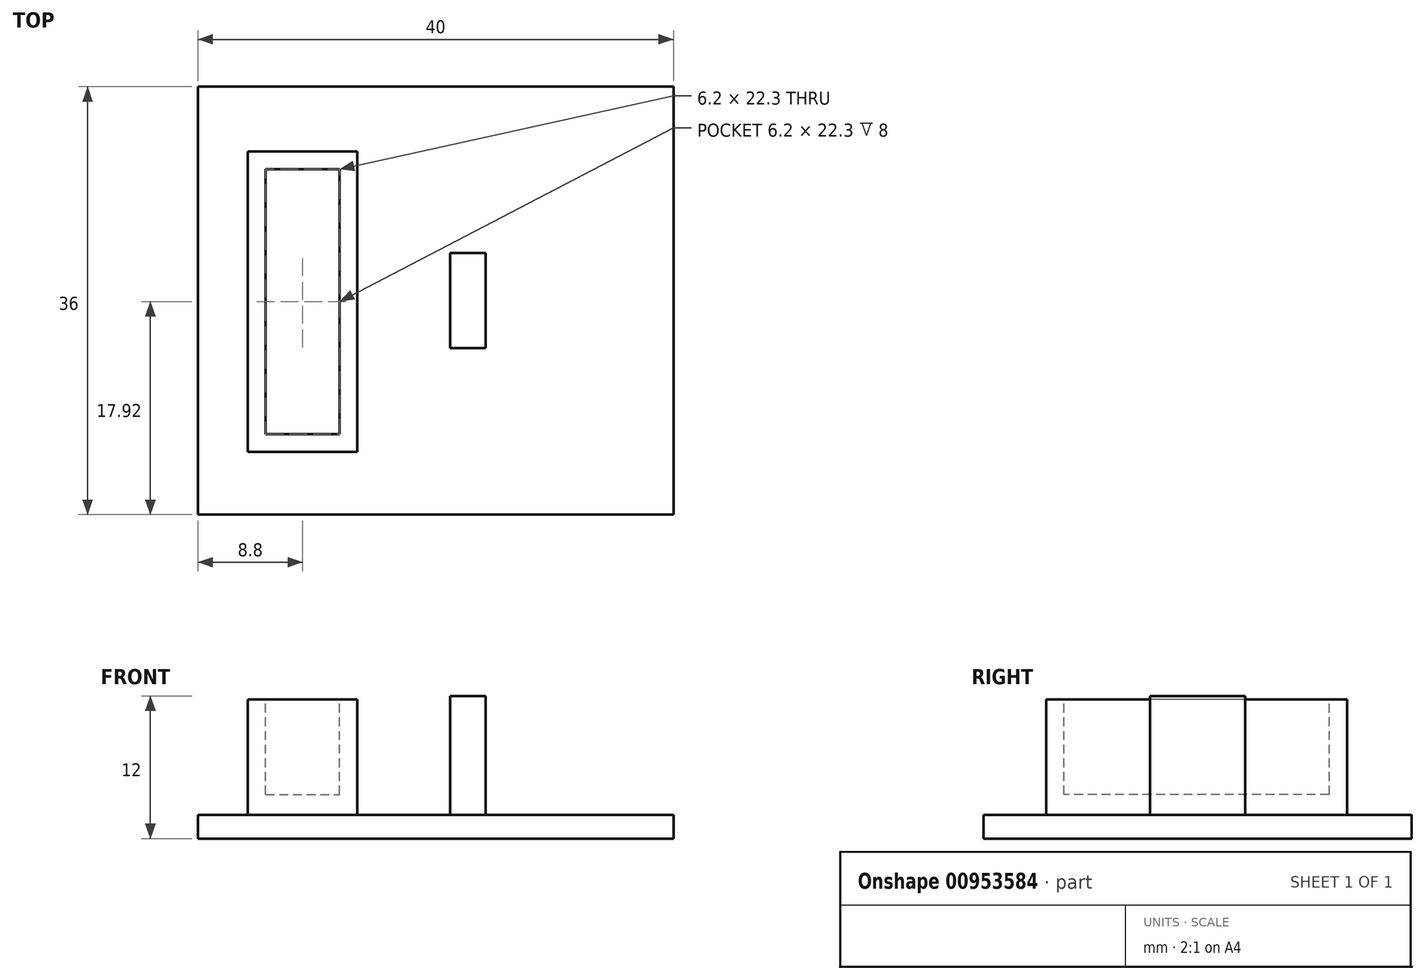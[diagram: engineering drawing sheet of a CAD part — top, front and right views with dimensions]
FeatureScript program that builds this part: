
annotation { "Feature Type Name" : "Feature", "Feature Type Description" : "" }
export const myFeature = defineFeature(function(context is Context, id is Id, definition is map)
    precondition{}
    {
        {
            var Q0;
            Q0=qCreatedBy(makeId("Top.planeOp"),FACE);
            var sketch = newSketch(context, id + "F0", { "sketchPlane" : qUnion([Q0])});
            skLineSegment(sketch, "E0.bottom", {"start": v(-20, 18) * mm, "end": v(20, 18) * mm});
            skLineSegment(sketch, "E0.top", {"start": v(-20, -18) * mm, "end": v(20, -18) * mm});
            skLineSegment(sketch, "E0.left", {"start": v(-20, 18) * mm, "end": v(-20, -18) * mm});
            skLineSegment(sketch, "E0.right", {"start": v(20, 18) * mm, "end": v(20, -18) * mm});
            skLineSegment(sketch, "E1", {"start": v(20, 18) * mm, "end": v(-20, -18) * mm, "construction": true});
            skLineSegment(sketch, "E2", {"start": v(-20, 18) * mm, "end": v(20, -18) * mm, "construction": true});
            skPoint(sketch, "E3", {"position": v(0, 0) * mm});
            skSolve(sketch);
        }
        {
            var Q0;
            Q0 = qSketchRegion(id + "F0", true);
            extrude(context, id + "F1", {"entities" : qUnion([Q0]), "depth" : 2 * mm, "offsetDistance" : 25 * mm});
        }
        {
            var Q0;
            Q0=makeQuery(id+"F1.opExtrude","CAP_FACE",FACE,{"disambiguationData":[OSD([sQuery(id+"F0.wireOp",EDGE,"E0.bottom"),sQuery(id+"F0.wireOp",EDGE,"E0.top"),sQuery(id+"F0.wireOp",EDGE,"E0.left"),sQuery(id+"F0.wireOp",EDGE,"E0.right")])],"isStart":false});
            var sketch = newSketch(context, id + "F2", { "sketchPlane" : qUnion([Q0])});
            skLineSegment(sketch, "E4.bottom", {"start": v(-15.8, 12.57) * mm, "end": v(-6.6, 12.57) * mm});
            skLineSegment(sketch, "E4.top", {"start": v(-15.8, -12.73) * mm, "end": v(-6.6, -12.73) * mm});
            skLineSegment(sketch, "E4.left", {"start": v(-15.8, 12.57) * mm, "end": v(-15.8, -12.73) * mm});
            skLineSegment(sketch, "E4.right", {"start": v(-6.6, 12.57) * mm, "end": v(-6.6, -12.73) * mm});
            skSolve(sketch);
        }
        {
            var Q0;
            Q0 = qSketchRegion(id + "F2", true);
            extrude(context, id + "F3", {"entities" : qUnion([Q0]), "depth" : 9.7 * mm, "offsetDistance" : 25 * mm});
        }
        {
            var Q0;
            Q0=makeQuery(id+"F3.opExtrude","CAP_FACE",FACE,{"disambiguationData":[OSD([sQuery(id+"F2.wireOp",EDGE,"E4.bottom"),sQuery(id+"F2.wireOp",EDGE,"E4.top"),sQuery(id+"F2.wireOp",EDGE,"E4.left"),sQuery(id+"F2.wireOp",EDGE,"E4.right")])],"isStart":false});
            var sketch = newSketch(context, id + "F4", { "sketchPlane" : qUnion([Q0])});
            skLineSegment(sketch, "E5.0", {"start": v(-14.3, 11.07) * mm, "end": v(-14.3, -11.23) * mm});
            skLineSegment(sketch, "E5.1", {"start": v(-14.3, 11.07) * mm, "end": v(-8.1, 11.07) * mm});
            skLineSegment(sketch, "E5.2", {"start": v(-8.1, 11.07) * mm, "end": v(-8.1, -11.23) * mm});
            skLineSegment(sketch, "E5.3", {"start": v(-14.3, -11.23) * mm, "end": v(-8.1, -11.23) * mm});
            skSolve(sketch);
        }
        {
            var Q0;
            Q0 = qSketchRegion(id + "F4", true);
            extrude(context, id + "F5", {"entities" : qUnion([Q0]), "operationType" : NewBodyOperationType.REMOVE, "oppositeDirection" : true, "depth" : 8 * mm, "offsetDistance" : 25 * mm});
        }
        {
            var Q0;
            Q0=makeQuery(id+"F1.opExtrude","CAP_FACE",FACE,{"disambiguationData":[OSD([sQuery(id+"F0.wireOp",EDGE,"E0.bottom"),sQuery(id+"F0.wireOp",EDGE,"E0.top"),sQuery(id+"F0.wireOp",EDGE,"E0.left"),sQuery(id+"F0.wireOp",EDGE,"E0.right")])],"isStart":false});
            var sketch = newSketch(context, id + "F6", { "sketchPlane" : qUnion([Q0])});
            skLineSegment(sketch, "E6.bottom", {"start": v(1.2, 4) * mm, "end": v(4.2, 4) * mm});
            skLineSegment(sketch, "E6.top", {"start": v(1.2, -4) * mm, "end": v(4.2, -4) * mm});
            skLineSegment(sketch, "E6.left", {"start": v(1.2, 4) * mm, "end": v(1.2, -4) * mm});
            skLineSegment(sketch, "E6.right", {"start": v(4.2, 4) * mm, "end": v(4.2, -4) * mm});
            skSolve(sketch);
        }
        {
            var Q0;
            Q0 = qSketchRegion(id + "F6", true);
            extrude(context, id + "F7", {"entities" : qUnion([Q0]), "depth" : 10 * mm, "offsetDistance" : 25 * mm});
        }
    });
